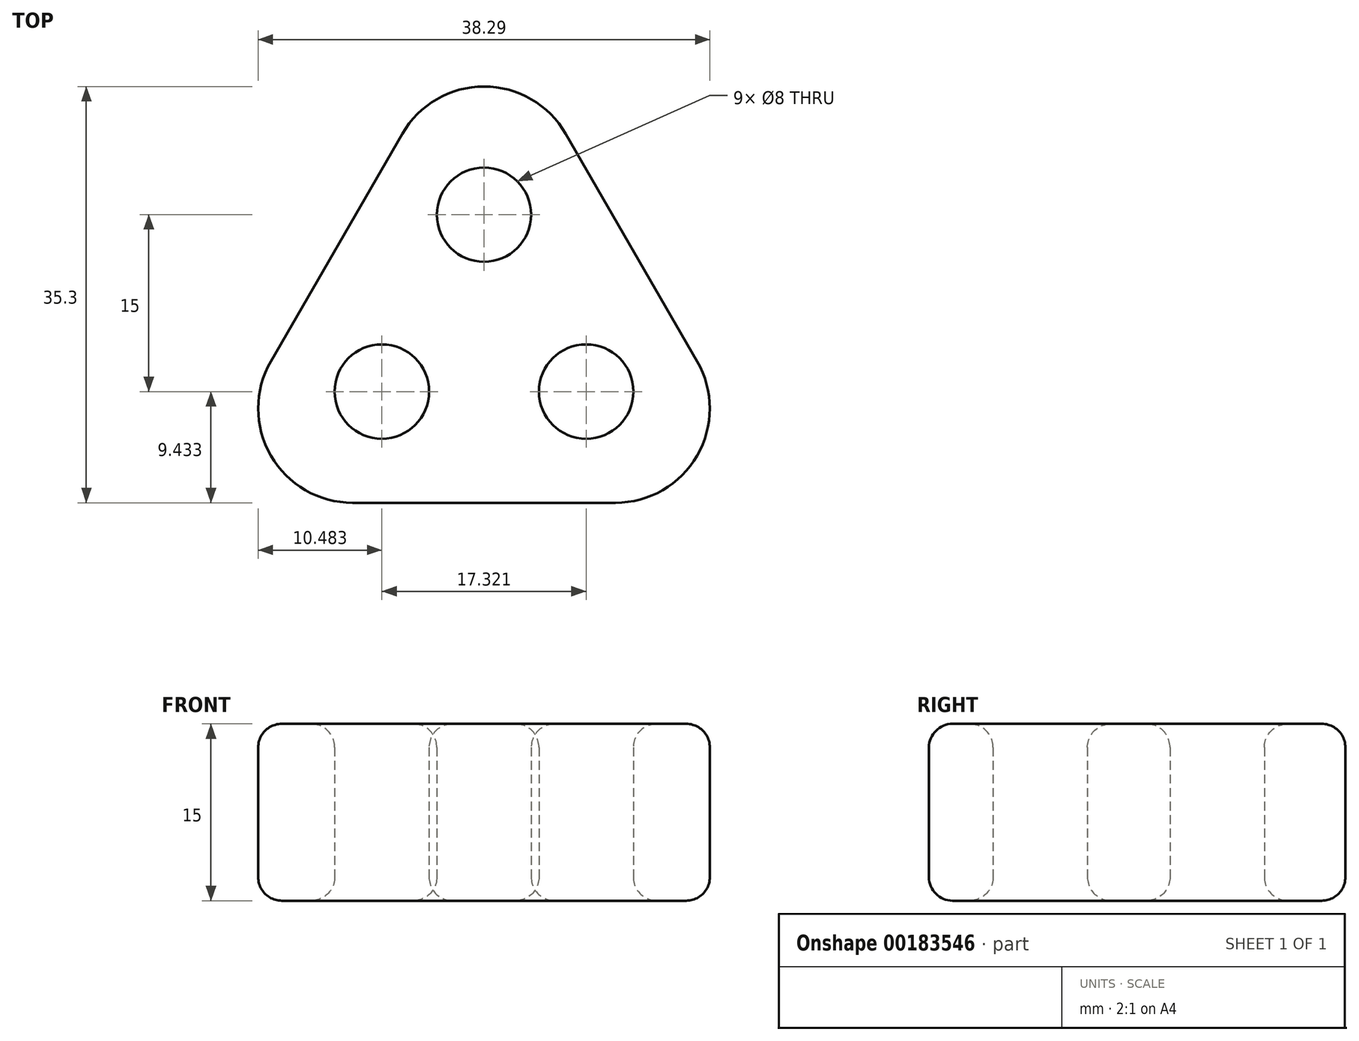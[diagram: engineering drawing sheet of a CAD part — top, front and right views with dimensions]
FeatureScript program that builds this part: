
annotation { "Feature Type Name" : "Feature", "Feature Type Description" : "" }
export const myFeature = defineFeature(function(context is Context, id is Id, definition is map)
    precondition{}
    {
        {
            var Q0;
            Q0=qCreatedBy(makeId("Top.planeOp"),FACE);
            var sketch = newSketch(context, id + "F0", { "sketchPlane" : qUnion([Q0])});
            skLineSegment(sketch, "E0", {"start": v(-11.05, -66.46) * mm, "end": v(38.95, -66.46) * mm});
            skLineSegment(sketch, "E1", {"start": v(38.95, -66.46) * mm, "end": v(13.95, -23.16) * mm});
            skLineSegment(sketch, "E2", {"start": v(13.95, -23.16) * mm, "end": v(-11.05, -66.46) * mm});
            skLineSegment(sketch, "E3", {"start": v(38.95, -66.46) * mm, "end": v(1.45, -44.81) * mm, "construction": true});
            skLineSegment(sketch, "E4", {"start": v(13.95, -66.46) * mm, "end": v(13.95, -23.16) * mm, "construction": true});
            skLineSegment(sketch, "E5", {"start": v(-11.05, -66.46) * mm, "end": v(26.45, -44.81) * mm, "construction": true});
            skLineSegment(sketch, "E6", {"start": v(13.95, -52.03) * mm, "end": v(22.61, -57.03) * mm});
            skLineSegment(sketch, "E7", {"start": v(13.95, -52.03) * mm, "end": v(5.3, -57.03) * mm});
            skLineSegment(sketch, "E8", {"start": v(13.95, -52.03) * mm, "end": v(13.95, -42.03) * mm});
            skCircle(sketch, "E9", {"center": v(5.3, -57.03) * mm, "radius": 4 * mm});
            skCircle(sketch, "E10", {"center": v(22.61, -57.03) * mm, "radius": 4 * mm});
            skCircle(sketch, "E11", {"center": v(13.95, -42.03) * mm, "radius": 4 * mm});
            skSolve(sketch);
        }
        {
            var Q0;
            Q0=makeQuery(id+"F0.imprint","IMPRINT",FACE,{"disambiguationData":[TD([[makeQuery(id+"F0.imprint","IMPRINT",EDGE,{"derivedFrom":sQuery(id+"F0.wireOp",EDGE,"E0")}),1.0]])]});
            extrude(context, id + "F1", {"entities" : qUnion([Q0]), "depth" : 15 * mm});
        }
        {
            var Q0;
            Q0=makeQuery(id+"F1.opExtrude","SWEPT_EDGE",EDGE,{"disambiguationData":[OSD([sQuery(id+"F0.wireOp",EDGE,"E0"),sQuery(id+"F0.wireOp",EDGE,"E1")])]});
            var Q1;
            Q1=makeQuery(id+"F1.opExtrude","SWEPT_EDGE",EDGE,{"disambiguationData":[OSD([sQuery(id+"F0.wireOp",EDGE,"E1"),sQuery(id+"F0.wireOp",EDGE,"E2")])]});
            var Q2;
            Q2=makeQuery(id+"F1.opExtrude","SWEPT_EDGE",EDGE,{"disambiguationData":[OSD([sQuery(id+"F0.wireOp",EDGE,"E0"),sQuery(id+"F0.wireOp",EDGE,"E2")])]});
            fillet(context, id + "F2", {"entities" : qUnion([Q0, Q1, Q2]), "radius" : 8 * mm, "tangentPropagation" : true, "allowEdgeOverflow" : false});
        }
        {
            var Q0;
            Q0=makeQuery(id+"F1.opExtrude","CAP_FACE",FACE,{"disambiguationData":[OSD([sQuery(id+"F0.wireOp",EDGE,"E0"),sQuery(id+"F0.wireOp",EDGE,"E1"),sQuery(id+"F0.wireOp",EDGE,"E2"),sQuery(id+"F0.wireOp",EDGE,"E9"),sQuery(id+"F0.wireOp",EDGE,"E10"),sQuery(id+"F0.wireOp",EDGE,"E11")])],"isStart":false});
            var Q1;
            Q1=makeQuery(id+"F1.opExtrude","CAP_FACE",FACE,{"disambiguationData":[OSD([sQuery(id+"F0.wireOp",EDGE,"E0"),sQuery(id+"F0.wireOp",EDGE,"E1"),sQuery(id+"F0.wireOp",EDGE,"E2"),sQuery(id+"F0.wireOp",EDGE,"E9"),sQuery(id+"F0.wireOp",EDGE,"E10"),sQuery(id+"F0.wireOp",EDGE,"E11")])],"isStart":true});
            fillet(context, id + "F3", {"entities" : qUnion([Q0, Q1]), "radius" : 2 * mm, "tangentPropagation" : true, "allowEdgeOverflow" : false});
        }
    });
